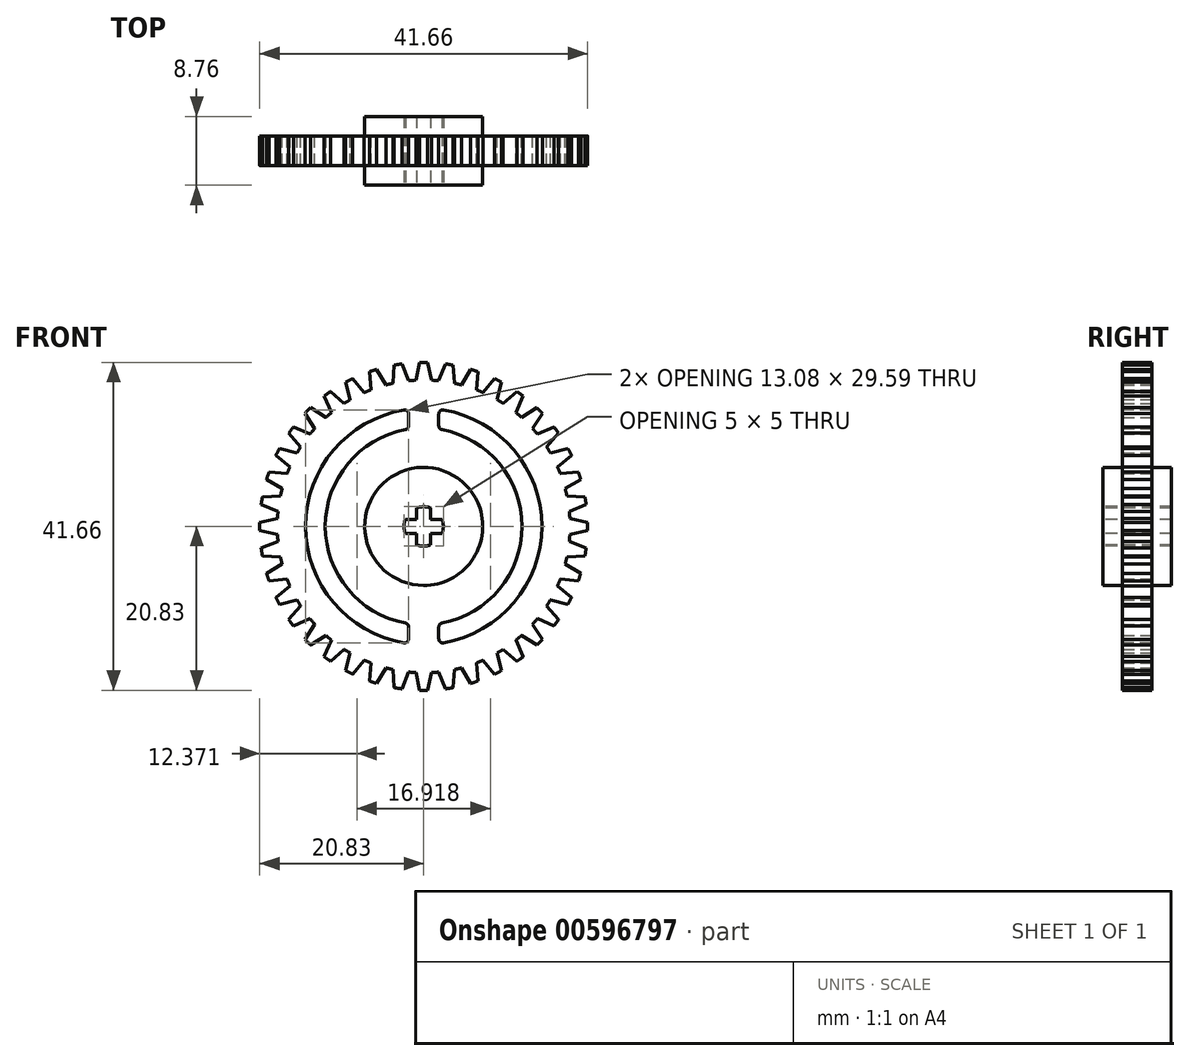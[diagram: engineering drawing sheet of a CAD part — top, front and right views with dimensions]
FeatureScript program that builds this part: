
annotation { "Feature Type Name" : "Feature", "Feature Type Description" : "" }
export const myFeature = defineFeature(function(context is Context, id is Id, definition is map)
    precondition{}
    {
        {
            var Q0;
            Q0=qCreatedBy(makeId("Front.planeOp"),FACE);
            var sketch = newSketch(context, id + "F0", { "sketchPlane" : qUnion([Q0])});
            skArc(sketch, "E0", {"start": v(0.5, 20.82) * mm, "mid": v(0, 20.82) * mm, "end": v(-0.5, 20.82) * mm});
            skCircle(sketch, "E1", {"center": v(0, 0) * mm, "radius": 18.6 * mm});
            skLineSegment(sketch, "E2", {"start": v(0, 20.82) * mm, "end": v(0, 18.6) * mm, "construction": true});
            skLineSegment(sketch, "E3", {"start": v(0, 18.6) * mm, "end": v(0, 15.8) * mm, "construction": true});
            skLineSegment(sketch, "E4", {"start": v(-1, 18.57) * mm, "end": v(0, 18.57) * mm, "construction": true});
            skLineSegment(sketch, "E5", {"start": v(0, 18.57) * mm, "end": v(1, 18.57) * mm, "construction": true});
            skLineSegment(sketch, "E6", {"start": v(0.98, 18.64) * mm, "end": v(1.03, 18.43) * mm});
            skLineSegment(sketch, "E7", {"start": v(-0.97, 18.7) * mm, "end": v(-1.04, 18.41) * mm});
            skLineSegment(sketch, "E8", {"start": v(0.5, 20.82) * mm, "end": v(1.02, 18.5) * mm});
            skLineSegment(sketch, "E9", {"start": v(-1.02, 18.5) * mm, "end": v(-0.5, 20.82) * mm});
            skCircle(sketch, "E10", {"center": v(0, 0) * mm, "radius": 7.5 * mm});
            skSolve(sketch);
        }
        {
            var Q0;
            Q0=qSketchRegion(id+"F0",true);
            extrude(context, id + "F1", {"entities" : qUnion([Q0]), "endBound" : BoundingType.SYMMETRIC, "depth" : 3.75 * mm, "offsetDistance" : 25 * mm});
        }
        {
            var Q0;
            Q0=makeQuery(id+"F1.opExtrude","CAP_FACE",FACE,{"disambiguationData":[OSD([sQuery(id+"F0.wireOp",EDGE,"E0"),sQuery(id+"F0.wireOp",EDGE,"E1"),sQuery(id+"F0.wireOp",EDGE,"E8"),sQuery(id+"F0.wireOp",EDGE,"E9")])],"isStart":false});
            var sketch = newSketch(context, id + "F2", { "sketchPlane" : qUnion([Q0])});
            skCircle(sketch, "E11", {"center": v(0, 0) * mm, "radius": 18.6 * mm});
            skLineSegment(sketch, "E12.0", {"start": v(0.5, 20.82) * mm, "end": v(1, 18.57) * mm});
            skLineSegment(sketch, "E13.0", {"start": v(-1, 18.57) * mm, "end": v(-0.5, 20.82) * mm});
            skArc(sketch, "E14.0", {"start": v(0.5, 20.82) * mm, "mid": v(0, 20.82) * mm, "end": v(-0.5, 20.82) * mm});
            skSolve(sketch);
        }
        {
            var Q0;
            Q0=makeQuery(id+"F1.opExtrude","SWEPT_BODY",BODY,{"disambiguationData":[OSD([sQuery(id+"F0.wireOp",EDGE,"E0"),sQuery(id+"F0.wireOp",EDGE,"E1"),sQuery(id+"F0.wireOp",EDGE,"E8"),sQuery(id+"F0.wireOp",EDGE,"E9")])]});
            var Q1;
            Q1=sQuery(id+"F2.wireOp",EDGE,"E11");
            circularPattern(context, id + "F3", {"entities" : qUnion([Q0]), "axis" : qUnion([Q1]), "angle" : 360 * degree, "instanceCount" : 40, "equalSpace" : true});
        }
        {
            var Q0;
            Q0=makeQuery(id+"F0.imprint","IMPRINT",FACE,{"disambiguationData":[TD([[makeQuery(id+"F0.imprint","IMPRINT",EDGE,{"derivedFrom":sQuery(id+"F0.wireOp",EDGE,"E10")}),1.0]])]});
            extrude(context, id + "F4", {"entities" : qUnion([Q0]), "endBound" : BoundingType.SYMMETRIC, "depth" : 8.75 * mm, "offsetDistance" : 25 * mm});
        }
        {
            var Q0;
            Q0=makeQuery(id+"F4.opExtrude","CAP_FACE",FACE,{"disambiguationData":[OSD([sQuery(id+"F0.wireOp",EDGE,"E10")])],"isStart":false});
            var sketch = newSketch(context, id + "F5", { "sketchPlane" : qUnion([Q0])});
            skCircle(sketch, "E15", {"center": v(0, 0) * mm, "radius": 2.5 * mm});
            skLineSegment(sketch, "E16", {"start": v(0, 0) * mm, "end": v(0, 0.9) * mm, "construction": true});
            skLineSegment(sketch, "E17", {"start": v(0, 0) * mm, "end": v(0, -0.9) * mm, "construction": true});
            skLineSegment(sketch, "E18", {"start": v(0, -0.9) * mm, "end": v(0, 0) * mm, "construction": true});
            skLineSegment(sketch, "E19", {"start": v(0, 0) * mm, "end": v(0.9, 0) * mm, "construction": true});
            skLineSegment(sketch, "E20", {"start": v(0, 0) * mm, "end": v(-0.9, 0) * mm, "construction": true});
            skLineSegment(sketch, "E21", {"start": v(-2.33, 0.9) * mm, "end": v(-0.9, 0.9) * mm});
            skLineSegment(sketch, "E22", {"start": v(0.9, 2.33) * mm, "end": v(0.9, 0.9) * mm});
            skLineSegment(sketch, "E23", {"start": v(2.33, -0.9) * mm, "end": v(0.9, -0.9) * mm});
            skLineSegment(sketch, "E24", {"start": v(-0.9, -2.33) * mm, "end": v(-0.9, -0.9) * mm});
            skLineSegment(sketch, "E25.trimOffspring", {"start": v(0.9, 0.9) * mm, "end": v(2.33, 0.9) * mm});
            skLineSegment(sketch, "E26.trimOffspring", {"start": v(0.9, -0.9) * mm, "end": v(0.9, -2.33) * mm});
            skLineSegment(sketch, "E27.trimOffspring", {"start": v(-0.9, -0.9) * mm, "end": v(-2.33, -0.9) * mm});
            skLineSegment(sketch, "E28.trimOffspring", {"start": v(-0.9, 0.9) * mm, "end": v(-0.9, 2.33) * mm});
            skSolve(sketch);
        }
        {
            var Q0;
            {var subQ4=sQuery(id+"F5.wireOp",EDGE,"E21");Q0=makeQuery(id+"F5.imprint","IMPRINT",FACE,{"disambiguationData":[TD([[makeQuery(id+"F5.imprint","IMPRINT",EDGE,{"derivedFrom":subQ4}),-1.0]])]});}
            extrude(context, id + "F6", {"entities" : qUnion([Q0]), "operationType" : NewBodyOperationType.REMOVE, "endBound" : BoundingType.THROUGH_ALL, "oppositeDirection" : true, "depth" : 25 * mm, "offsetDistance" : 25 * mm});
        }
        {
            var Q0;
            Q0=makeQuery(id+"F3.opPattern","COPY",BODY,{"derivedFrom":makeQuery(id+"F1.opExtrude","SWEPT_BODY",BODY,{"disambiguationData":[OSD([sQuery(id+"F0.wireOp",EDGE,"E0"),sQuery(id+"F0.wireOp",EDGE,"E1"),sQuery(id+"F0.wireOp",EDGE,"E8"),sQuery(id+"F0.wireOp",EDGE,"E9"),sQuery(id+"F0.wireOp",EDGE,"E10")])]}),"instanceName":"12"});
            var Q1;
            Q1=makeQuery(id+"F3.opPattern","COPY",BODY,{"derivedFrom":makeQuery(id+"F1.opExtrude","SWEPT_BODY",BODY,{"disambiguationData":[OSD([sQuery(id+"F0.wireOp",EDGE,"E0"),sQuery(id+"F0.wireOp",EDGE,"E1"),sQuery(id+"F0.wireOp",EDGE,"E8"),sQuery(id+"F0.wireOp",EDGE,"E9"),sQuery(id+"F0.wireOp",EDGE,"E10")])]}),"instanceName":"16"});
            var Q2;
            Q2=makeQuery(id+"F3.opPattern","COPY",BODY,{"derivedFrom":makeQuery(id+"F1.opExtrude","SWEPT_BODY",BODY,{"disambiguationData":[OSD([sQuery(id+"F0.wireOp",EDGE,"E0"),sQuery(id+"F0.wireOp",EDGE,"E1"),sQuery(id+"F0.wireOp",EDGE,"E8"),sQuery(id+"F0.wireOp",EDGE,"E9"),sQuery(id+"F0.wireOp",EDGE,"E10")])]}),"instanceName":"11"});
            var Q3;
            Q3=makeQuery(id+"F3.opPattern","COPY",BODY,{"derivedFrom":makeQuery(id+"F1.opExtrude","SWEPT_BODY",BODY,{"disambiguationData":[OSD([sQuery(id+"F0.wireOp",EDGE,"E0"),sQuery(id+"F0.wireOp",EDGE,"E1"),sQuery(id+"F0.wireOp",EDGE,"E8"),sQuery(id+"F0.wireOp",EDGE,"E9"),sQuery(id+"F0.wireOp",EDGE,"E10")])]}),"instanceName":"10"});
            var Q4;
            Q4=makeQuery(id+"F3.opPattern","COPY",BODY,{"derivedFrom":makeQuery(id+"F1.opExtrude","SWEPT_BODY",BODY,{"disambiguationData":[OSD([sQuery(id+"F0.wireOp",EDGE,"E0"),sQuery(id+"F0.wireOp",EDGE,"E1"),sQuery(id+"F0.wireOp",EDGE,"E8"),sQuery(id+"F0.wireOp",EDGE,"E9"),sQuery(id+"F0.wireOp",EDGE,"E10")])]}),"instanceName":"9"});
            var Q5;
            Q5=makeQuery(id+"F3.opPattern","COPY",BODY,{"derivedFrom":makeQuery(id+"F1.opExtrude","SWEPT_BODY",BODY,{"disambiguationData":[OSD([sQuery(id+"F0.wireOp",EDGE,"E0"),sQuery(id+"F0.wireOp",EDGE,"E1"),sQuery(id+"F0.wireOp",EDGE,"E8"),sQuery(id+"F0.wireOp",EDGE,"E9"),sQuery(id+"F0.wireOp",EDGE,"E10")])]}),"instanceName":"8"});
            var Q6;
            Q6=makeQuery(id+"F3.opPattern","COPY",BODY,{"derivedFrom":makeQuery(id+"F1.opExtrude","SWEPT_BODY",BODY,{"disambiguationData":[OSD([sQuery(id+"F0.wireOp",EDGE,"E0"),sQuery(id+"F0.wireOp",EDGE,"E1"),sQuery(id+"F0.wireOp",EDGE,"E8"),sQuery(id+"F0.wireOp",EDGE,"E9"),sQuery(id+"F0.wireOp",EDGE,"E10")])]}),"instanceName":"7"});
            var Q7;
            Q7=makeQuery(id+"F3.opPattern","COPY",BODY,{"derivedFrom":makeQuery(id+"F1.opExtrude","SWEPT_BODY",BODY,{"disambiguationData":[OSD([sQuery(id+"F0.wireOp",EDGE,"E0"),sQuery(id+"F0.wireOp",EDGE,"E1"),sQuery(id+"F0.wireOp",EDGE,"E8"),sQuery(id+"F0.wireOp",EDGE,"E9"),sQuery(id+"F0.wireOp",EDGE,"E10")])]}),"instanceName":"6"});
            var Q8;
            Q8=makeQuery(id+"F3.opPattern","COPY",BODY,{"derivedFrom":makeQuery(id+"F1.opExtrude","SWEPT_BODY",BODY,{"disambiguationData":[OSD([sQuery(id+"F0.wireOp",EDGE,"E0"),sQuery(id+"F0.wireOp",EDGE,"E1"),sQuery(id+"F0.wireOp",EDGE,"E8"),sQuery(id+"F0.wireOp",EDGE,"E9"),sQuery(id+"F0.wireOp",EDGE,"E10")])]}),"instanceName":"5"});
            var Q9;
            Q9=makeQuery(id+"F3.opPattern","COPY",BODY,{"derivedFrom":makeQuery(id+"F1.opExtrude","SWEPT_BODY",BODY,{"disambiguationData":[OSD([sQuery(id+"F0.wireOp",EDGE,"E0"),sQuery(id+"F0.wireOp",EDGE,"E1"),sQuery(id+"F0.wireOp",EDGE,"E8"),sQuery(id+"F0.wireOp",EDGE,"E9"),sQuery(id+"F0.wireOp",EDGE,"E10")])]}),"instanceName":"4"});
            var Q10;
            Q10=makeQuery(id+"F3.opPattern","COPY",BODY,{"derivedFrom":makeQuery(id+"F1.opExtrude","SWEPT_BODY",BODY,{"disambiguationData":[OSD([sQuery(id+"F0.wireOp",EDGE,"E0"),sQuery(id+"F0.wireOp",EDGE,"E1"),sQuery(id+"F0.wireOp",EDGE,"E8"),sQuery(id+"F0.wireOp",EDGE,"E9"),sQuery(id+"F0.wireOp",EDGE,"E10")])]}),"instanceName":"3"});
            var Q11;
            Q11=makeQuery(id+"F3.opPattern","COPY",BODY,{"derivedFrom":makeQuery(id+"F1.opExtrude","SWEPT_BODY",BODY,{"disambiguationData":[OSD([sQuery(id+"F0.wireOp",EDGE,"E0"),sQuery(id+"F0.wireOp",EDGE,"E1"),sQuery(id+"F0.wireOp",EDGE,"E8"),sQuery(id+"F0.wireOp",EDGE,"E9"),sQuery(id+"F0.wireOp",EDGE,"E10")])]}),"instanceName":"2"});
            var Q12;
            Q12=makeQuery(id+"F3.opPattern","COPY",BODY,{"derivedFrom":makeQuery(id+"F1.opExtrude","SWEPT_BODY",BODY,{"disambiguationData":[OSD([sQuery(id+"F0.wireOp",EDGE,"E0"),sQuery(id+"F0.wireOp",EDGE,"E1"),sQuery(id+"F0.wireOp",EDGE,"E8"),sQuery(id+"F0.wireOp",EDGE,"E9"),sQuery(id+"F0.wireOp",EDGE,"E10")])]}),"instanceName":"1"});
            var Q13;
            Q13=makeQuery(id+"F1.opExtrude","SWEPT_BODY",BODY,{"disambiguationData":[OSD([sQuery(id+"F0.wireOp",EDGE,"E0"),sQuery(id+"F0.wireOp",EDGE,"E1"),sQuery(id+"F0.wireOp",EDGE,"E8"),sQuery(id+"F0.wireOp",EDGE,"E9"),sQuery(id+"F0.wireOp",EDGE,"E10")])]});
            var Q14;
            Q14=makeQuery(id+"F3.opPattern","COPY",BODY,{"derivedFrom":makeQuery(id+"F1.opExtrude","SWEPT_BODY",BODY,{"disambiguationData":[OSD([sQuery(id+"F0.wireOp",EDGE,"E0"),sQuery(id+"F0.wireOp",EDGE,"E1"),sQuery(id+"F0.wireOp",EDGE,"E8"),sQuery(id+"F0.wireOp",EDGE,"E9"),sQuery(id+"F0.wireOp",EDGE,"E10")])]}),"instanceName":"15"});
            var Q15;
            Q15=makeQuery(id+"F3.opPattern","COPY",BODY,{"derivedFrom":makeQuery(id+"F1.opExtrude","SWEPT_BODY",BODY,{"disambiguationData":[OSD([sQuery(id+"F0.wireOp",EDGE,"E0"),sQuery(id+"F0.wireOp",EDGE,"E1"),sQuery(id+"F0.wireOp",EDGE,"E8"),sQuery(id+"F0.wireOp",EDGE,"E9"),sQuery(id+"F0.wireOp",EDGE,"E10")])]}),"instanceName":"14"});
            var Q16;
            Q16=makeQuery(id+"F3.opPattern","COPY",BODY,{"derivedFrom":makeQuery(id+"F1.opExtrude","SWEPT_BODY",BODY,{"disambiguationData":[OSD([sQuery(id+"F0.wireOp",EDGE,"E0"),sQuery(id+"F0.wireOp",EDGE,"E1"),sQuery(id+"F0.wireOp",EDGE,"E8"),sQuery(id+"F0.wireOp",EDGE,"E9"),sQuery(id+"F0.wireOp",EDGE,"E10")])]}),"instanceName":"13"});
            var Q17;
            Q17=makeQuery(id+"F3.opPattern","COPY",BODY,{"derivedFrom":makeQuery(id+"F1.opExtrude","SWEPT_BODY",BODY,{"disambiguationData":[OSD([sQuery(id+"F0.wireOp",EDGE,"E0"),sQuery(id+"F0.wireOp",EDGE,"E1"),sQuery(id+"F0.wireOp",EDGE,"E8"),sQuery(id+"F0.wireOp",EDGE,"E9"),sQuery(id+"F0.wireOp",EDGE,"E10")])]}),"instanceName":"24"});
            var Q18;
            Q18=makeQuery(id+"F3.opPattern","COPY",BODY,{"derivedFrom":makeQuery(id+"F1.opExtrude","SWEPT_BODY",BODY,{"disambiguationData":[OSD([sQuery(id+"F0.wireOp",EDGE,"E0"),sQuery(id+"F0.wireOp",EDGE,"E1"),sQuery(id+"F0.wireOp",EDGE,"E8"),sQuery(id+"F0.wireOp",EDGE,"E9"),sQuery(id+"F0.wireOp",EDGE,"E10")])]}),"instanceName":"25"});
            var Q19;
            Q19=makeQuery(id+"F3.opPattern","COPY",BODY,{"derivedFrom":makeQuery(id+"F1.opExtrude","SWEPT_BODY",BODY,{"disambiguationData":[OSD([sQuery(id+"F0.wireOp",EDGE,"E0"),sQuery(id+"F0.wireOp",EDGE,"E1"),sQuery(id+"F0.wireOp",EDGE,"E8"),sQuery(id+"F0.wireOp",EDGE,"E9"),sQuery(id+"F0.wireOp",EDGE,"E10")])]}),"instanceName":"26"});
            var Q20;
            Q20=makeQuery(id+"F3.opPattern","COPY",BODY,{"derivedFrom":makeQuery(id+"F1.opExtrude","SWEPT_BODY",BODY,{"disambiguationData":[OSD([sQuery(id+"F0.wireOp",EDGE,"E0"),sQuery(id+"F0.wireOp",EDGE,"E1"),sQuery(id+"F0.wireOp",EDGE,"E8"),sQuery(id+"F0.wireOp",EDGE,"E9"),sQuery(id+"F0.wireOp",EDGE,"E10")])]}),"instanceName":"27"});
            var Q21;
            Q21=makeQuery(id+"F3.opPattern","COPY",BODY,{"derivedFrom":makeQuery(id+"F1.opExtrude","SWEPT_BODY",BODY,{"disambiguationData":[OSD([sQuery(id+"F0.wireOp",EDGE,"E0"),sQuery(id+"F0.wireOp",EDGE,"E1"),sQuery(id+"F0.wireOp",EDGE,"E8"),sQuery(id+"F0.wireOp",EDGE,"E9"),sQuery(id+"F0.wireOp",EDGE,"E10")])]}),"instanceName":"28"});
            var Q22;
            Q22=makeQuery(id+"F3.opPattern","COPY",BODY,{"derivedFrom":makeQuery(id+"F1.opExtrude","SWEPT_BODY",BODY,{"disambiguationData":[OSD([sQuery(id+"F0.wireOp",EDGE,"E0"),sQuery(id+"F0.wireOp",EDGE,"E1"),sQuery(id+"F0.wireOp",EDGE,"E8"),sQuery(id+"F0.wireOp",EDGE,"E9"),sQuery(id+"F0.wireOp",EDGE,"E10")])]}),"instanceName":"29"});
            var Q23;
            Q23=makeQuery(id+"F3.opPattern","COPY",BODY,{"derivedFrom":makeQuery(id+"F1.opExtrude","SWEPT_BODY",BODY,{"disambiguationData":[OSD([sQuery(id+"F0.wireOp",EDGE,"E0"),sQuery(id+"F0.wireOp",EDGE,"E1"),sQuery(id+"F0.wireOp",EDGE,"E8"),sQuery(id+"F0.wireOp",EDGE,"E9"),sQuery(id+"F0.wireOp",EDGE,"E10")])]}),"instanceName":"30"});
            var Q24;
            Q24=makeQuery(id+"F3.opPattern","COPY",BODY,{"derivedFrom":makeQuery(id+"F1.opExtrude","SWEPT_BODY",BODY,{"disambiguationData":[OSD([sQuery(id+"F0.wireOp",EDGE,"E0"),sQuery(id+"F0.wireOp",EDGE,"E1"),sQuery(id+"F0.wireOp",EDGE,"E8"),sQuery(id+"F0.wireOp",EDGE,"E9"),sQuery(id+"F0.wireOp",EDGE,"E10")])]}),"instanceName":"31"});
            var Q25;
            Q25=makeQuery(id+"F3.opPattern","COPY",BODY,{"derivedFrom":makeQuery(id+"F1.opExtrude","SWEPT_BODY",BODY,{"disambiguationData":[OSD([sQuery(id+"F0.wireOp",EDGE,"E0"),sQuery(id+"F0.wireOp",EDGE,"E1"),sQuery(id+"F0.wireOp",EDGE,"E8"),sQuery(id+"F0.wireOp",EDGE,"E9"),sQuery(id+"F0.wireOp",EDGE,"E10")])]}),"instanceName":"32"});
            var Q26;
            Q26=makeQuery(id+"F3.opPattern","COPY",BODY,{"derivedFrom":makeQuery(id+"F1.opExtrude","SWEPT_BODY",BODY,{"disambiguationData":[OSD([sQuery(id+"F0.wireOp",EDGE,"E0"),sQuery(id+"F0.wireOp",EDGE,"E1"),sQuery(id+"F0.wireOp",EDGE,"E8"),sQuery(id+"F0.wireOp",EDGE,"E9"),sQuery(id+"F0.wireOp",EDGE,"E10")])]}),"instanceName":"33"});
            var Q27;
            Q27=makeQuery(id+"F3.opPattern","COPY",BODY,{"derivedFrom":makeQuery(id+"F1.opExtrude","SWEPT_BODY",BODY,{"disambiguationData":[OSD([sQuery(id+"F0.wireOp",EDGE,"E0"),sQuery(id+"F0.wireOp",EDGE,"E1"),sQuery(id+"F0.wireOp",EDGE,"E8"),sQuery(id+"F0.wireOp",EDGE,"E9"),sQuery(id+"F0.wireOp",EDGE,"E10")])]}),"instanceName":"34"});
            var Q28;
            Q28=makeQuery(id+"F3.opPattern","COPY",BODY,{"derivedFrom":makeQuery(id+"F1.opExtrude","SWEPT_BODY",BODY,{"disambiguationData":[OSD([sQuery(id+"F0.wireOp",EDGE,"E0"),sQuery(id+"F0.wireOp",EDGE,"E1"),sQuery(id+"F0.wireOp",EDGE,"E8"),sQuery(id+"F0.wireOp",EDGE,"E9"),sQuery(id+"F0.wireOp",EDGE,"E10")])]}),"instanceName":"35"});
            var Q29;
            Q29=makeQuery(id+"F3.opPattern","COPY",BODY,{"derivedFrom":makeQuery(id+"F1.opExtrude","SWEPT_BODY",BODY,{"disambiguationData":[OSD([sQuery(id+"F0.wireOp",EDGE,"E0"),sQuery(id+"F0.wireOp",EDGE,"E1"),sQuery(id+"F0.wireOp",EDGE,"E8"),sQuery(id+"F0.wireOp",EDGE,"E9"),sQuery(id+"F0.wireOp",EDGE,"E10")])]}),"instanceName":"36"});
            var Q30;
            Q30=makeQuery(id+"F3.opPattern","COPY",BODY,{"derivedFrom":makeQuery(id+"F1.opExtrude","SWEPT_BODY",BODY,{"disambiguationData":[OSD([sQuery(id+"F0.wireOp",EDGE,"E0"),sQuery(id+"F0.wireOp",EDGE,"E1"),sQuery(id+"F0.wireOp",EDGE,"E8"),sQuery(id+"F0.wireOp",EDGE,"E9"),sQuery(id+"F0.wireOp",EDGE,"E10")])]}),"instanceName":"37"});
            var Q31;
            Q31=makeQuery(id+"F3.opPattern","COPY",BODY,{"derivedFrom":makeQuery(id+"F1.opExtrude","SWEPT_BODY",BODY,{"disambiguationData":[OSD([sQuery(id+"F0.wireOp",EDGE,"E0"),sQuery(id+"F0.wireOp",EDGE,"E1"),sQuery(id+"F0.wireOp",EDGE,"E8"),sQuery(id+"F0.wireOp",EDGE,"E9"),sQuery(id+"F0.wireOp",EDGE,"E10")])]}),"instanceName":"38"});
            var Q32;
            Q32=makeQuery(id+"F3.opPattern","COPY",BODY,{"derivedFrom":makeQuery(id+"F1.opExtrude","SWEPT_BODY",BODY,{"disambiguationData":[OSD([sQuery(id+"F0.wireOp",EDGE,"E0"),sQuery(id+"F0.wireOp",EDGE,"E1"),sQuery(id+"F0.wireOp",EDGE,"E8"),sQuery(id+"F0.wireOp",EDGE,"E9"),sQuery(id+"F0.wireOp",EDGE,"E10")])]}),"instanceName":"39"});
            var Q33;
            Q33=makeQuery(id+"F4.opExtrude","SWEPT_BODY",BODY,{"disambiguationData":[OSD([sQuery(id+"F0.wireOp",EDGE,"E10")])]});
            var Q34;
            Q34=makeQuery(id+"F3.opPattern","COPY",BODY,{"derivedFrom":makeQuery(id+"F1.opExtrude","SWEPT_BODY",BODY,{"disambiguationData":[OSD([sQuery(id+"F0.wireOp",EDGE,"E0"),sQuery(id+"F0.wireOp",EDGE,"E1"),sQuery(id+"F0.wireOp",EDGE,"E8"),sQuery(id+"F0.wireOp",EDGE,"E9"),sQuery(id+"F0.wireOp",EDGE,"E10")])]}),"instanceName":"17"});
            var Q35;
            Q35=makeQuery(id+"F3.opPattern","COPY",BODY,{"derivedFrom":makeQuery(id+"F1.opExtrude","SWEPT_BODY",BODY,{"disambiguationData":[OSD([sQuery(id+"F0.wireOp",EDGE,"E0"),sQuery(id+"F0.wireOp",EDGE,"E1"),sQuery(id+"F0.wireOp",EDGE,"E8"),sQuery(id+"F0.wireOp",EDGE,"E9"),sQuery(id+"F0.wireOp",EDGE,"E10")])]}),"instanceName":"18"});
            var Q36;
            Q36=makeQuery(id+"F3.opPattern","COPY",BODY,{"derivedFrom":makeQuery(id+"F1.opExtrude","SWEPT_BODY",BODY,{"disambiguationData":[OSD([sQuery(id+"F0.wireOp",EDGE,"E0"),sQuery(id+"F0.wireOp",EDGE,"E1"),sQuery(id+"F0.wireOp",EDGE,"E8"),sQuery(id+"F0.wireOp",EDGE,"E9"),sQuery(id+"F0.wireOp",EDGE,"E10")])]}),"instanceName":"19"});
            var Q37;
            Q37=makeQuery(id+"F3.opPattern","COPY",BODY,{"derivedFrom":makeQuery(id+"F1.opExtrude","SWEPT_BODY",BODY,{"disambiguationData":[OSD([sQuery(id+"F0.wireOp",EDGE,"E0"),sQuery(id+"F0.wireOp",EDGE,"E1"),sQuery(id+"F0.wireOp",EDGE,"E8"),sQuery(id+"F0.wireOp",EDGE,"E9"),sQuery(id+"F0.wireOp",EDGE,"E10")])]}),"instanceName":"23"});
            var Q38;
            Q38=makeQuery(id+"F3.opPattern","COPY",BODY,{"derivedFrom":makeQuery(id+"F1.opExtrude","SWEPT_BODY",BODY,{"disambiguationData":[OSD([sQuery(id+"F0.wireOp",EDGE,"E0"),sQuery(id+"F0.wireOp",EDGE,"E1"),sQuery(id+"F0.wireOp",EDGE,"E8"),sQuery(id+"F0.wireOp",EDGE,"E9"),sQuery(id+"F0.wireOp",EDGE,"E10")])]}),"instanceName":"20"});
            var Q39;
            Q39=makeQuery(id+"F3.opPattern","COPY",BODY,{"derivedFrom":makeQuery(id+"F1.opExtrude","SWEPT_BODY",BODY,{"disambiguationData":[OSD([sQuery(id+"F0.wireOp",EDGE,"E0"),sQuery(id+"F0.wireOp",EDGE,"E1"),sQuery(id+"F0.wireOp",EDGE,"E8"),sQuery(id+"F0.wireOp",EDGE,"E9"),sQuery(id+"F0.wireOp",EDGE,"E10")])]}),"instanceName":"21"});
            var Q40;
            Q40=makeQuery(id+"F3.opPattern","COPY",BODY,{"derivedFrom":makeQuery(id+"F1.opExtrude","SWEPT_BODY",BODY,{"disambiguationData":[OSD([sQuery(id+"F0.wireOp",EDGE,"E0"),sQuery(id+"F0.wireOp",EDGE,"E1"),sQuery(id+"F0.wireOp",EDGE,"E8"),sQuery(id+"F0.wireOp",EDGE,"E9"),sQuery(id+"F0.wireOp",EDGE,"E10")])]}),"instanceName":"22"});
            booleanBodies(context, id + "F7", {"operationType" : BooleanOperationType.UNION, "tools" : qUnion([Q0, Q1, Q2, Q3, Q4, Q5, Q6, Q7, Q8, Q9, Q10, Q11, Q12, Q13, Q14, Q15, Q16, Q17, Q18, Q19, Q20, Q21, Q22, Q23, Q24, Q25, Q26, Q27, Q28, Q29, Q30, Q31, Q32, Q33, Q34, Q35, Q36, Q37, Q38, Q39, Q40])});
        }
        {
            var Q0;
            {var subQ0=makeQuery(id+"F1.opExtrude","CAP_FACE",FACE,{"disambiguationData":[OSD([sQuery(id+"F0.wireOp",EDGE,"E0"),sQuery(id+"F0.wireOp",EDGE,"E1"),sQuery(id+"F0.wireOp",EDGE,"E8"),sQuery(id+"F0.wireOp",EDGE,"E9"),sQuery(id+"F0.wireOp",EDGE,"E10")])],"isStart":false});Q0=makeQuery(id+"F7.opBoolean","MERGE",FACE,{"derivedFrom":[subQ0,makeQuery(id+"F3.opPattern","COPY",FACE,{"derivedFrom":subQ0,"instanceName":"1"}),makeQuery(id+"F3.opPattern","COPY",FACE,{"derivedFrom":subQ0,"instanceName":"2"}),makeQuery(id+"F3.opPattern","COPY",FACE,{"derivedFrom":subQ0,"instanceName":"3"}),makeQuery(id+"F3.opPattern","COPY",FACE,{"derivedFrom":subQ0,"instanceName":"4"}),makeQuery(id+"F3.opPattern","COPY",FACE,{"derivedFrom":subQ0,"instanceName":"5"}),makeQuery(id+"F3.opPattern","COPY",FACE,{"derivedFrom":subQ0,"instanceName":"6"}),makeQuery(id+"F3.opPattern","COPY",FACE,{"derivedFrom":subQ0,"instanceName":"7"}),makeQuery(id+"F3.opPattern","COPY",FACE,{"derivedFrom":subQ0,"instanceName":"8"}),makeQuery(id+"F3.opPattern","COPY",FACE,{"derivedFrom":subQ0,"instanceName":"9"}),makeQuery(id+"F3.opPattern","COPY",FACE,{"derivedFrom":subQ0,"instanceName":"10"}),makeQuery(id+"F3.opPattern","COPY",FACE,{"derivedFrom":subQ0,"instanceName":"11"}),makeQuery(id+"F3.opPattern","COPY",FACE,{"derivedFrom":subQ0,"instanceName":"12"}),makeQuery(id+"F3.opPattern","COPY",FACE,{"derivedFrom":subQ0,"instanceName":"13"}),makeQuery(id+"F3.opPattern","COPY",FACE,{"derivedFrom":subQ0,"instanceName":"14"}),makeQuery(id+"F3.opPattern","COPY",FACE,{"derivedFrom":subQ0,"instanceName":"15"}),makeQuery(id+"F3.opPattern","COPY",FACE,{"derivedFrom":subQ0,"instanceName":"16"}),makeQuery(id+"F3.opPattern","COPY",FACE,{"derivedFrom":subQ0,"instanceName":"17"}),makeQuery(id+"F3.opPattern","COPY",FACE,{"derivedFrom":subQ0,"instanceName":"18"}),makeQuery(id+"F3.opPattern","COPY",FACE,{"derivedFrom":subQ0,"instanceName":"19"}),makeQuery(id+"F3.opPattern","COPY",FACE,{"derivedFrom":subQ0,"instanceName":"20"}),makeQuery(id+"F3.opPattern","COPY",FACE,{"derivedFrom":subQ0,"instanceName":"21"}),makeQuery(id+"F3.opPattern","COPY",FACE,{"derivedFrom":subQ0,"instanceName":"22"}),makeQuery(id+"F3.opPattern","COPY",FACE,{"derivedFrom":subQ0,"instanceName":"23"}),makeQuery(id+"F3.opPattern","COPY",FACE,{"derivedFrom":subQ0,"instanceName":"24"}),makeQuery(id+"F3.opPattern","COPY",FACE,{"derivedFrom":subQ0,"instanceName":"25"}),makeQuery(id+"F3.opPattern","COPY",FACE,{"derivedFrom":subQ0,"instanceName":"26"}),makeQuery(id+"F3.opPattern","COPY",FACE,{"derivedFrom":subQ0,"instanceName":"27"}),makeQuery(id+"F3.opPattern","COPY",FACE,{"derivedFrom":subQ0,"instanceName":"28"}),makeQuery(id+"F3.opPattern","COPY",FACE,{"derivedFrom":subQ0,"instanceName":"29"}),makeQuery(id+"F3.opPattern","COPY",FACE,{"derivedFrom":subQ0,"instanceName":"30"}),makeQuery(id+"F3.opPattern","COPY",FACE,{"derivedFrom":subQ0,"instanceName":"31"}),makeQuery(id+"F3.opPattern","COPY",FACE,{"derivedFrom":subQ0,"instanceName":"32"}),makeQuery(id+"F3.opPattern","COPY",FACE,{"derivedFrom":subQ0,"instanceName":"33"}),makeQuery(id+"F3.opPattern","COPY",FACE,{"derivedFrom":subQ0,"instanceName":"34"}),makeQuery(id+"F3.opPattern","COPY",FACE,{"derivedFrom":subQ0,"instanceName":"35"}),makeQuery(id+"F3.opPattern","COPY",FACE,{"derivedFrom":subQ0,"instanceName":"36"}),makeQuery(id+"F3.opPattern","COPY",FACE,{"derivedFrom":subQ0,"instanceName":"37"}),makeQuery(id+"F3.opPattern","COPY",FACE,{"derivedFrom":subQ0,"instanceName":"38"}),makeQuery(id+"F3.opPattern","COPY",FACE,{"derivedFrom":subQ0,"instanceName":"39"})]});}
            var sketch = newSketch(context, id + "F8", { "sketchPlane" : qUnion([Q0])});
            skArc(sketch, "E29", {"start": v(-2.5, 14.8) * mm, "mid": v(-15, 0) * mm, "end": v(-2.5, -14.8) * mm});
            skArc(sketch, "E30", {"start": v(-2.32, 12.28) * mm, "mid": v(-12.5, 0) * mm, "end": v(-2.32, -12.28) * mm});
            skLineSegment(sketch, "E31", {"start": v(1.92, -14.3) * mm, "end": v(1.92, -12.77) * mm});
            skLineSegment(sketch, "E32", {"start": v(-1.92, -14.3) * mm, "end": v(-1.92, -12.77) * mm});
            skLineSegment(sketch, "E33", {"start": v(-1.92, 14.3) * mm, "end": v(-1.92, 12.77) * mm});
            skLineSegment(sketch, "E34", {"start": v(1.92, 14.3) * mm, "end": v(1.92, 12.77) * mm});
            skArc(sketch, "E35.trimOffspring", {"start": v(2.32, -12.28) * mm, "mid": v(12.5, 0) * mm, "end": v(2.32, 12.28) * mm});
            skArc(sketch, "E36.trimOffspring", {"start": v(2.5, -14.8) * mm, "mid": v(15, 0) * mm, "end": v(2.5, 14.8) * mm});
            skPoint(sketch, "E37.visualSharp", {"position": v(-1.92, -12.35) * mm});
            skArc(sketch, "E37.filletArc", {"start": v(-1.92, -12.77) * mm, "mid": v(-2.03, -12.45) * mm, "end": v(-2.32, -12.28) * mm});
            skPoint(sketch, "E38.visualSharp", {"position": v(-1.92, -14.88) * mm});
            skArc(sketch, "E38.filletArc", {"start": v(-2.5, -14.8) * mm, "mid": v(-2.1, -14.68) * mm, "end": v(-1.92, -14.3) * mm});
            skPoint(sketch, "E39.visualSharp", {"position": v(1.92, -12.35) * mm});
            skArc(sketch, "E39.filletArc", {"start": v(2.32, -12.28) * mm, "mid": v(2.03, -12.45) * mm, "end": v(1.92, -12.77) * mm});
            skPoint(sketch, "E40.visualSharp", {"position": v(1.92, -14.88) * mm});
            skArc(sketch, "E40.filletArc", {"start": v(1.92, -14.3) * mm, "mid": v(2.1, -14.68) * mm, "end": v(2.5, -14.8) * mm});
            skPoint(sketch, "E41.visualSharp", {"position": v(-1.92, 14.88) * mm});
            skArc(sketch, "E41.filletArc", {"start": v(-1.92, 14.3) * mm, "mid": v(-2.1, 14.68) * mm, "end": v(-2.5, 14.8) * mm});
            skPoint(sketch, "E42.visualSharp", {"position": v(-1.92, 12.35) * mm});
            skArc(sketch, "E42.filletArc", {"start": v(-2.32, 12.28) * mm, "mid": v(-2.03, 12.45) * mm, "end": v(-1.92, 12.77) * mm});
            skPoint(sketch, "E43.visualSharp", {"position": v(1.92, 14.88) * mm});
            skArc(sketch, "E43.filletArc", {"start": v(2.5, 14.8) * mm, "mid": v(2.1, 14.68) * mm, "end": v(1.92, 14.3) * mm});
            skPoint(sketch, "E44.visualSharp", {"position": v(1.92, 12.35) * mm});
            skArc(sketch, "E44.filletArc", {"start": v(1.92, 12.77) * mm, "mid": v(2.03, 12.45) * mm, "end": v(2.32, 12.28) * mm});
            skSolve(sketch);
        }
        {
            var Q0;
            Q0=qSketchRegion(id+"F8",true);
            extrude(context, id + "F9", {"entities" : qUnion([Q0]), "operationType" : NewBodyOperationType.REMOVE, "endBound" : BoundingType.THROUGH_ALL, "oppositeDirection" : true, "depth" : 25 * mm, "offsetDistance" : 25 * mm});
        }
    });
